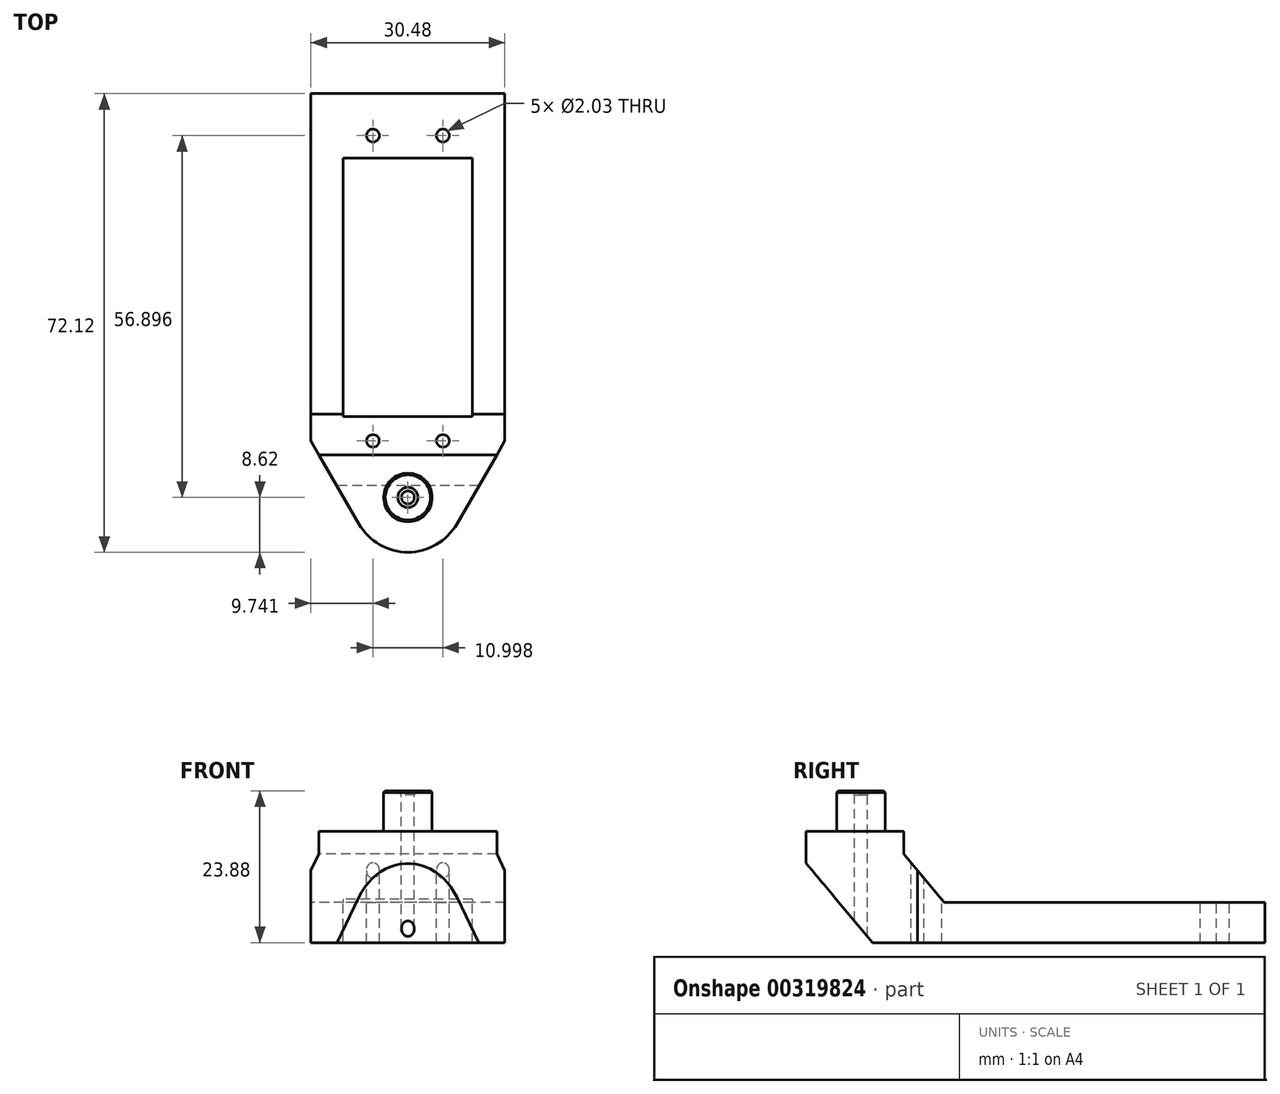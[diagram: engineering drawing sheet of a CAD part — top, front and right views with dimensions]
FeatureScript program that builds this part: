
annotation { "Feature Type Name" : "Feature", "Feature Type Description" : "" }
export const myFeature = defineFeature(function(context is Context, id is Id, definition is map)
    precondition{}
    {
        {
            var Q0;
            Q0=qCreatedBy(makeId("Top.planeOp"),FACE);
            var sketch = newSketch(context, id + "F0", { "sketchPlane" : qUnion([Q0])});
            skLineSegment(sketch, "E0", {"start": v(0, 0) * mm, "end": v(0, -22.86) * mm, "construction": true});
            skCircle(sketch, "E1", {"center": v(0, 0) * mm, "radius": 6.35 * mm, "construction": true});
            skLineSegment(sketch, "E2.bottom", {"start": v(10.16, -10.16) * mm, "end": v(-10.16, -10.16) * mm});
            skLineSegment(sketch, "E2.top", {"start": v(10.16, 30.48) * mm, "end": v(-10.16, 30.48) * mm});
            skLineSegment(sketch, "E2.left", {"start": v(10.16, -10.16) * mm, "end": v(10.16, 30.48) * mm});
            skLineSegment(sketch, "E2.right", {"start": v(-10.16, -10.16) * mm, "end": v(-10.16, 30.48) * mm});
            skPoint(sketch, "E2.middle", {"position": v(0, 10.16) * mm});
            skLineSegment(sketch, "E3.bottom", {"start": v(-15.24, 40.64) * mm, "end": v(15.24, 40.64) * mm});
            skLineSegment(sketch, "E3.top", {"start": v(-15.24, -13.97) * mm, "end": v(15.24, -13.97) * mm, "construction": true});
            skLineSegment(sketch, "E3.left", {"start": v(-15.24, 40.64) * mm, "end": v(-15.24, -13.97) * mm});
            skLineSegment(sketch, "E3.right", {"start": v(15.24, 40.64) * mm, "end": v(15.24, -13.97) * mm});
            skCircle(sketch, "E4", {"center": v(0, -22.86) * mm, "radius": 3.81 * mm, "construction": true});
            skArc(sketch, "E5", {"start": v(7.7, -27.03) * mm, "mid": v(0, -31.48) * mm, "end": v(-7.7, -27.03) * mm});
            skLineSegment(sketch, "E6", {"start": v(7.7, -27.03) * mm, "end": v(15.24, -13.97) * mm});
            skLineSegment(sketch, "E7", {"start": v(-7.7, -27.03) * mm, "end": v(-15.24, -13.97) * mm});
            skPoint(sketch, "E8", {"position": v(-5.5, 34.04) * mm});
            skPoint(sketch, "E9", {"position": v(5.5, 34.04) * mm});
            skPoint(sketch, "E10", {"position": v(-5.5, -13.97) * mm});
            skPoint(sketch, "E11", {"position": v(5.5, -13.97) * mm});
            skCircle(sketch, "E12", {"center": v(5.5, 34.04) * mm, "radius": 1.02 * mm});
            skCircle(sketch, "E13", {"center": v(-5.5, 34.04) * mm, "radius": 1.02 * mm});
            skCircle(sketch, "E14", {"center": v(5.5, -13.97) * mm, "radius": 1.02 * mm});
            skCircle(sketch, "E15", {"center": v(-5.5, -13.97) * mm, "radius": 1.02 * mm});
            skSolve(sketch);
        }
        {
            var Q0;
            Q0=qCreatedBy(makeId("Right.planeOp"),FACE);
            var sketch = newSketch(context, id + "F1", { "sketchPlane" : qUnion([Q0])});
            skLineSegment(sketch, "E16", {"start": v(-31.48, 0) * mm, "end": v(-31.48, -5.06) * mm});
            skLineSegment(sketch, "E17", {"start": v(-31.48, -5.06) * mm, "end": v(-21.02, -17.53) * mm});
            skLineSegment(sketch, "E18", {"start": v(-21.02, -17.53) * mm, "end": v(40.64, -17.53) * mm});
            skLineSegment(sketch, "E19", {"start": v(40.64, -17.53) * mm, "end": v(40.64, -11.18) * mm});
            skLineSegment(sketch, "E20", {"start": v(40.64, -11.18) * mm, "end": v(-9.77, -11.18) * mm});
            skLineSegment(sketch, "E21", {"start": v(-9.77, -11.18) * mm, "end": v(-16.16, -3.56) * mm});
            skLineSegment(sketch, "E22", {"start": v(-16.16, -3.56) * mm, "end": v(-16.16, 0) * mm});
            skLineSegment(sketch, "E23", {"start": v(-16.16, 0) * mm, "end": v(-31.48, 0) * mm});
            skSolve(sketch);
        }
        {
            var Q0;
            Q0=makeQuery(id+"F0.imprint","IMPRINT",FACE,{"disambiguationData":[TD([[makeQuery(id+"F0.imprint","IMPRINT",EDGE,{"derivedFrom":sQuery(id+"F0.wireOp",EDGE,"E2.bottom")}),1.0]])]});
            var Q1;
            Q1=sQuery(id+"F1.wireOp",VERTEX,"E18.start");
            extrude(context, id + "F2", {"entities" : qUnion([Q0]), "endBound" : BoundingType.UP_TO_VERTEX, "oppositeDirection" : true, "endBoundEntityVertex" : qUnion([Q1]), "depth" : 25.4 * mm});
        }
        {
            var Q0;
            Q0 = qSketchRegion(id + "F1", true);
            extrude(context, id + "F3", {"entities" : qUnion([Q0]), "operationType" : NewBodyOperationType.INTERSECT, "endBound" : BoundingType.SYMMETRIC, "depth" : 127 * mm});
        }
        {
            var Q0;
            Q0=makeQuery(id+"F0.imprint","IMPRINT",FACE,{"disambiguationData":[TD([[makeQuery(id+"F0.imprint","IMPRINT",EDGE,{"derivedFrom":sQuery(id+"F0.wireOp",EDGE,"E2.bottom")}),1.0]])]});
            var sketch = newSketch(context, id + "F4", { "sketchPlane" : qUnion([Q0])});
            skCircle(sketch, "E24", {"center": v(0, -22.86) * mm, "radius": 3.8 * mm});
            skSolve(sketch);
        }
        {
            var Q0;
            Q0 = qSketchRegion(id + "F4", true);
            extrude(context, id + "F5", {"entities" : qUnion([Q0]), "operationType" : NewBodyOperationType.ADD, "depth" : 6.35 * mm});
        }
        {
            var Q0;
            Q0=makeQuery(id+"F5.opExtrude","CAP_FACE",FACE,{"disambiguationData":[OSD([sQuery(id+"F4.wireOp",EDGE,"E24")])],"isStart":false});
            var sketch = newSketch(context, id + "F6", { "sketchPlane" : qUnion([Q0])});
            skPoint(sketch, "E25", {"position": v(0, -22.86) * mm});
            skSolve(sketch);
        }
        {
            var Q0;
            Q0=sQuery(id+"F6.wireOp",VERTEX,"E25");
            var Q1;
            Q1=makeQuery(id+"F2.opExtrude","SWEPT_BODY",BODY,{"disambiguationData":[OSD([sQuery(id+"F0.wireOp",EDGE,"E2.bottom"),sQuery(id+"F0.wireOp",EDGE,"E2.top"),sQuery(id+"F0.wireOp",EDGE,"E2.left"),sQuery(id+"F0.wireOp",EDGE,"E2.right"),sQuery(id+"F0.wireOp",EDGE,"E3.bottom"),sQuery(id+"F0.wireOp",EDGE,"E3.left"),sQuery(id+"F0.wireOp",EDGE,"E3.right"),sQuery(id+"F0.wireOp",EDGE,"E5"),sQuery(id+"F0.wireOp",EDGE,"E6"),sQuery(id+"F0.wireOp",EDGE,"E7"),sQuery(id+"F0.wireOp",EDGE,"E12"),sQuery(id+"F0.wireOp",EDGE,"E13"),sQuery(id+"F0.wireOp",EDGE,"E14"),sQuery(id+"F0.wireOp",EDGE,"E15")])]});
            hole(context, id + "F7", {"style" : HoleStyle.C_SINK, "endStyle" : HoleEndStyle.THROUGH, "holeDiameter" : 2.03 * mm, "cSinkDiameter" : 3.17 * mm, "cSinkAngle" : 82 * degree, "tappedDepth" : 12.7 * mm, "tapClearance" : 3, "locations" : qUnion([Q0]), "scope" : qUnion([Q1])});
        }
        {
            var Q0;
            Q0=makeQuery(id+"F5.opExtrude","CAP_EDGE",EDGE,{"disambiguationData":[OSD([sQuery(id+"F4.wireOp",EDGE,"E24")])],"isStart":false});
            chamfer(context, id + "F8", {"entities" : qUnion([Q0]), "width" : 0.25 * mm, "tangentPropagation" : true});
        }
    });
